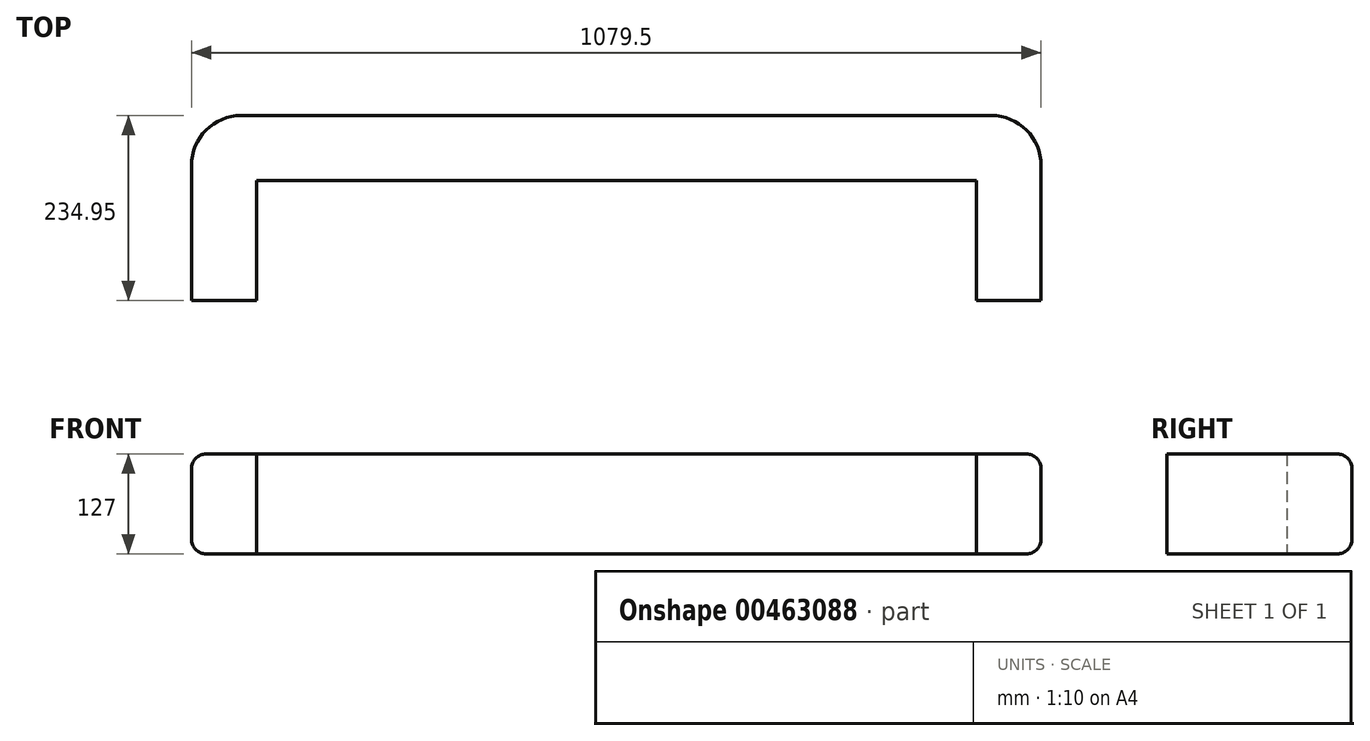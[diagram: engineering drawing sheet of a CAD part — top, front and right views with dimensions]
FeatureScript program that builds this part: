
annotation { "Feature Type Name" : "Feature", "Feature Type Description" : "" }
export const myFeature = defineFeature(function(context is Context, id is Id, definition is map)
    precondition{}
    {
        {
            var Q0;
            Q0=qCreatedBy(makeId("Front.planeOp"),FACE);
            var sketch = newSketch(context, id + "F0", { "sketchPlane" : qUnion([Q0])});
            skLineSegment(sketch, "E0.bottom", {"start": v(-41.93, 90.93) * mm, "end": v(872.47, 90.93) * mm});
            skLineSegment(sketch, "E0.top", {"start": v(-41.93, -36.07) * mm, "end": v(872.47, -36.07) * mm});
            skLineSegment(sketch, "E0.left", {"start": v(-41.93, 90.93) * mm, "end": v(-41.93, -36.07) * mm});
            skLineSegment(sketch, "E0.right", {"start": v(872.47, 90.93) * mm, "end": v(872.47, -36.07) * mm});
            skSolve(sketch);
        }
        {
            var Q0;
            Q0 = qSketchRegion(id + "F0", true);
            extrude(context, id + "F1", {"entities" : qUnion([Q0]), "depth" : 19.05 * mm});
        }
        {
            var Q0;
            Q0=makeQuery(id+"F1.opExtrude","SWEPT_FACE",FACE,{"disambiguationData":[OSD([sQuery(id+"F0.wireOp",EDGE,"E0.left")])]});
            var sketch = newSketch(context, id + "F2", { "sketchPlane" : qUnion([Q0])});
            skLineSegment(sketch, "E1.bottom", {"start": v(0, 90.93) * mm, "end": v(171.45, 90.93) * mm});
            skLineSegment(sketch, "E1.top", {"start": v(0, -36.07) * mm, "end": v(171.45, -36.07) * mm});
            skLineSegment(sketch, "E1.left", {"start": v(0, 90.93) * mm, "end": v(0, -36.07) * mm});
            skLineSegment(sketch, "E1.right", {"start": v(171.45, 90.93) * mm, "end": v(171.45, -36.07) * mm});
            skSolve(sketch);
        }
        {
            var Q0;
            Q0 = qSketchRegion(id + "F2", true);
            extrude(context, id + "F3", {"entities" : qUnion([Q0]), "operationType" : NewBodyOperationType.ADD, "depth" : 19.05 * mm});
        }
        {
            var Q0;
            Q0=makeQuery(id+"F1.opExtrude","SWEPT_FACE",FACE,{"disambiguationData":[OSD([sQuery(id+"F0.wireOp",EDGE,"E0.right")])]});
            var sketch = newSketch(context, id + "F4", { "sketchPlane" : qUnion([Q0])});
            skLineSegment(sketch, "E2.bottom", {"start": v(0, 90.93) * mm, "end": v(-171.45, 90.93) * mm});
            skLineSegment(sketch, "E2.top", {"start": v(0, -36.07) * mm, "end": v(-171.45, -36.07) * mm});
            skLineSegment(sketch, "E2.left", {"start": v(0, 90.93) * mm, "end": v(0, -36.07) * mm});
            skLineSegment(sketch, "E2.right", {"start": v(-171.45, 90.93) * mm, "end": v(-171.45, -36.07) * mm});
            skSolve(sketch);
        }
        {
            var Q0;
            Q0 = qSketchRegion(id + "F4", true);
            extrude(context, id + "F5", {"entities" : qUnion([Q0]), "operationType" : NewBodyOperationType.ADD, "depth" : 19.05 * mm});
        }
        {
            var Q0;
            Q0=qCreatedBy(makeId("Front.planeOp"),FACE);
            var sketch = newSketch(context, id + "F6", { "sketchPlane" : qUnion([Q0])});
            skLineSegment(sketch, "E3.bottom", {"start": v(-105.43, 90.93) * mm, "end": v(-60.98, 90.93) * mm});
            skLineSegment(sketch, "E3.top", {"start": v(-105.43, -36.07) * mm, "end": v(-60.98, -36.07) * mm});
            skLineSegment(sketch, "E3.left", {"start": v(-124.48, 71.88) * mm, "end": v(-124.48, -17.02) * mm});
            skLineSegment(sketch, "E3.right", {"start": v(-60.98, 90.93) * mm, "end": v(-60.98, -36.07) * mm});
            skPoint(sketch, "E4.visualSharp", {"position": v(-124.48, -36.07) * mm});
            skArc(sketch, "E4.filletArc", {"start": v(-124.48, -17.02) * mm, "mid": v(-118.9, -30.49) * mm, "end": v(-105.43, -36.07) * mm});
            skPoint(sketch, "E5.visualSharp", {"position": v(-124.48, 90.93) * mm});
            skArc(sketch, "E5.filletArc", {"start": v(-105.43, 90.93) * mm, "mid": v(-118.9, 85.35) * mm, "end": v(-124.48, 71.88) * mm});
            skSolve(sketch);
        }
        {
            var Q0;
            Q0 = qSketchRegion(id + "F6", true);
            extrude(context, id + "F7", {"entities" : qUnion([Q0]), "operationType" : NewBodyOperationType.ADD, "depth" : 171.45 * mm});
        }
        {
            var Q0;
            Q0 = qSketchRegion(id + "F6", true);
            var Q1;
            Q1=sQuery(id+"F6.wireOp",EDGE,"E3.right");
            revolve(context, id + "F8", {"operationType" : NewBodyOperationType.ADD, "entities" : qUnion([Q0]), "axis" : qUnion([Q1]), "revolveType" : RevolveType.ONE_DIRECTION, "angle" : 90 * degree});
        }
        {
            var Q0;
            Q0=makeQuery(id+"F8.opRevolve","CAP_FACE",FACE,{"disambiguationData":[OSD([sQuery(id+"F6.wireOp",EDGE,"E3.bottom"),sQuery(id+"F6.wireOp",EDGE,"E3.top"),sQuery(id+"F6.wireOp",EDGE,"E3.left"),sQuery(id+"F6.wireOp",EDGE,"E3.right"),sQuery(id+"F6.wireOp",EDGE,"E4.filletArc"),sQuery(id+"F6.wireOp",EDGE,"E5.filletArc")])],"isStart":false});
            var sketch = newSketch(context, id + "F9", { "sketchPlane" : qUnion([Q0])});
            skLineSegment(sketch, "E6.bottom", {"start": v(0, 90.93) * mm, "end": v(63.5, 90.93) * mm});
            skLineSegment(sketch, "E6.top", {"start": v(0, -36.07) * mm, "end": v(63.5, -36.07) * mm});
            skLineSegment(sketch, "E6.left", {"start": v(0, 90.93) * mm, "end": v(0, -36.07) * mm});
            skLineSegment(sketch, "E6.right", {"start": v(63.5, 90.93) * mm, "end": v(63.5, -36.07) * mm});
            skSolve(sketch);
        }
        {
            var Q0;
            Q0 = qSketchRegion(id + "F9", true);
            extrude(context, id + "F10", {"entities" : qUnion([Q0]), "operationType" : NewBodyOperationType.ADD, "depth" : 952.5 * mm});
        }
        {
            var Q0;
            Q0=makeQuery(id+"F10.opExtrude","SWEPT_EDGE",EDGE,{"disambiguationData":[OSD([sQuery(id+"F9.wireOp",EDGE,"E6.bottom"),sQuery(id+"F9.wireOp",EDGE,"E6.right")])]});
            var Q1;
            Q1=makeQuery(id+"F10.opExtrude","SWEPT_EDGE",EDGE,{"disambiguationData":[OSD([sQuery(id+"F9.wireOp",EDGE,"E6.top"),sQuery(id+"F9.wireOp",EDGE,"E6.right")])]});
            fillet(context, id + "F11", {"entities" : qUnion([Q0, Q1]), "radius" : 19.05 * mm, "tangentPropagation" : true, "allowEdgeOverflow" : false});
        }
        {
            var Q0;
            Q0=makeQuery(id+"F10.boolean.opBoolean","MERGE",FACE,{"derivedFrom":[makeQuery(id+"F5.opExtrude","CAP_FACE",FACE,{"disambiguationData":[OSD([sQuery(id+"F4.wireOp",EDGE,"E2.bottom"),sQuery(id+"F4.wireOp",EDGE,"E2.top"),sQuery(id+"F4.wireOp",EDGE,"E2.left"),sQuery(id+"F4.wireOp",EDGE,"E2.right")])],"isStart":false}),makeQuery(id+"F10.opExtrude","CAP_FACE",FACE,{"disambiguationData":[OSD([sQuery(id+"F9.wireOp",EDGE,"E6.bottom"),sQuery(id+"F9.wireOp",EDGE,"E6.top"),sQuery(id+"F9.wireOp",EDGE,"E6.left"),sQuery(id+"F9.wireOp",EDGE,"E6.right")])],"isStart":false})]});
            var sketch = newSketch(context, id + "F12", { "sketchPlane" : qUnion([Q0])});
            skLineSegment(sketch, "E7.bottom", {"start": v(0, -36.07) * mm, "end": v(63.5, -36.07) * mm});
            skLineSegment(sketch, "E7.top", {"start": v(0, 90.93) * mm, "end": v(63.5, 90.93) * mm});
            skLineSegment(sketch, "E7.left", {"start": v(0, -36.07) * mm, "end": v(0, 90.93) * mm});
            skLineSegment(sketch, "E7.right", {"start": v(63.5, -36.07) * mm, "end": v(63.5, 90.93) * mm});
            skSolve(sketch);
        }
        {
            var Q0;
            Q0 = qSketchRegion(id + "F12", true);
            var Q1;
            Q1=sQuery(id+"F12.wireOp",EDGE,"E7.left");
            revolve(context, id + "F13", {"operationType" : NewBodyOperationType.ADD, "entities" : qUnion([Q0]), "axis" : qUnion([Q1]), "revolveType" : RevolveType.ONE_DIRECTION, "oppositeDirection" : true, "angle" : 90 * degree});
        }
        {
            var Q0;
            Q0=makeQuery(id+"F13.opRevolve","SWEPT_EDGE",EDGE,{"disambiguationData":[OSD([sQuery(id+"F12.wireOp",EDGE,"E7.top"),sQuery(id+"F12.wireOp",EDGE,"E7.right")])]});
            var Q1;
            Q1=makeQuery(id+"F13.opRevolve","SWEPT_EDGE",EDGE,{"disambiguationData":[OSD([sQuery(id+"F12.wireOp",EDGE,"E7.bottom"),sQuery(id+"F12.wireOp",EDGE,"E7.right")])]});
            fillet(context, id + "F14", {"entities" : qUnion([Q0, Q1]), "radius" : 19.05 * mm, "tangentPropagation" : true, "allowEdgeOverflow" : false});
        }
        {
            var Q0;
            Q0=makeQuery(id+"F13.opRevolve","CAP_FACE",FACE,{"disambiguationData":[OSD([sQuery(id+"F12.wireOp",EDGE,"E7.bottom"),sQuery(id+"F12.wireOp",EDGE,"E7.top"),sQuery(id+"F12.wireOp",EDGE,"E7.left"),sQuery(id+"F12.wireOp",EDGE,"E7.right")])],"isStart":false});
            var sketch = newSketch(context, id + "F15", { "sketchPlane" : qUnion([Q0])});
            skLineSegment(sketch, "E8.bottom", {"start": v(891.52, -36.07) * mm, "end": v(955.02, -36.07) * mm});
            skLineSegment(sketch, "E8.top", {"start": v(891.52, 90.93) * mm, "end": v(955.02, 90.93) * mm});
            skLineSegment(sketch, "E8.left", {"start": v(891.52, -36.07) * mm, "end": v(891.52, 90.93) * mm});
            skLineSegment(sketch, "E8.right", {"start": v(955.02, -36.07) * mm, "end": v(955.02, 90.93) * mm});
            skSolve(sketch);
        }
        {
            var Q0;
            Q0 = qSketchRegion(id + "F15", true);
            extrude(context, id + "F16", {"entities" : qUnion([Q0]), "operationType" : NewBodyOperationType.ADD, "depth" : 171.45 * mm});
        }
        {
            var Q0;
            Q0=makeQuery(id+"F16.opExtrude","SWEPT_EDGE",EDGE,{"disambiguationData":[OSD([sQuery(id+"F15.wireOp",EDGE,"E8.top"),sQuery(id+"F15.wireOp",EDGE,"E8.right")])]});
            var Q1;
            Q1=makeQuery(id+"F16.opExtrude","SWEPT_EDGE",EDGE,{"disambiguationData":[OSD([sQuery(id+"F15.wireOp",EDGE,"E8.bottom"),sQuery(id+"F15.wireOp",EDGE,"E8.right")])]});
            fillet(context, id + "F17", {"entities" : qUnion([Q0, Q1]), "radius" : 19.05 * mm, "tangentPropagation" : true, "allowEdgeOverflow" : false});
        }
    });
